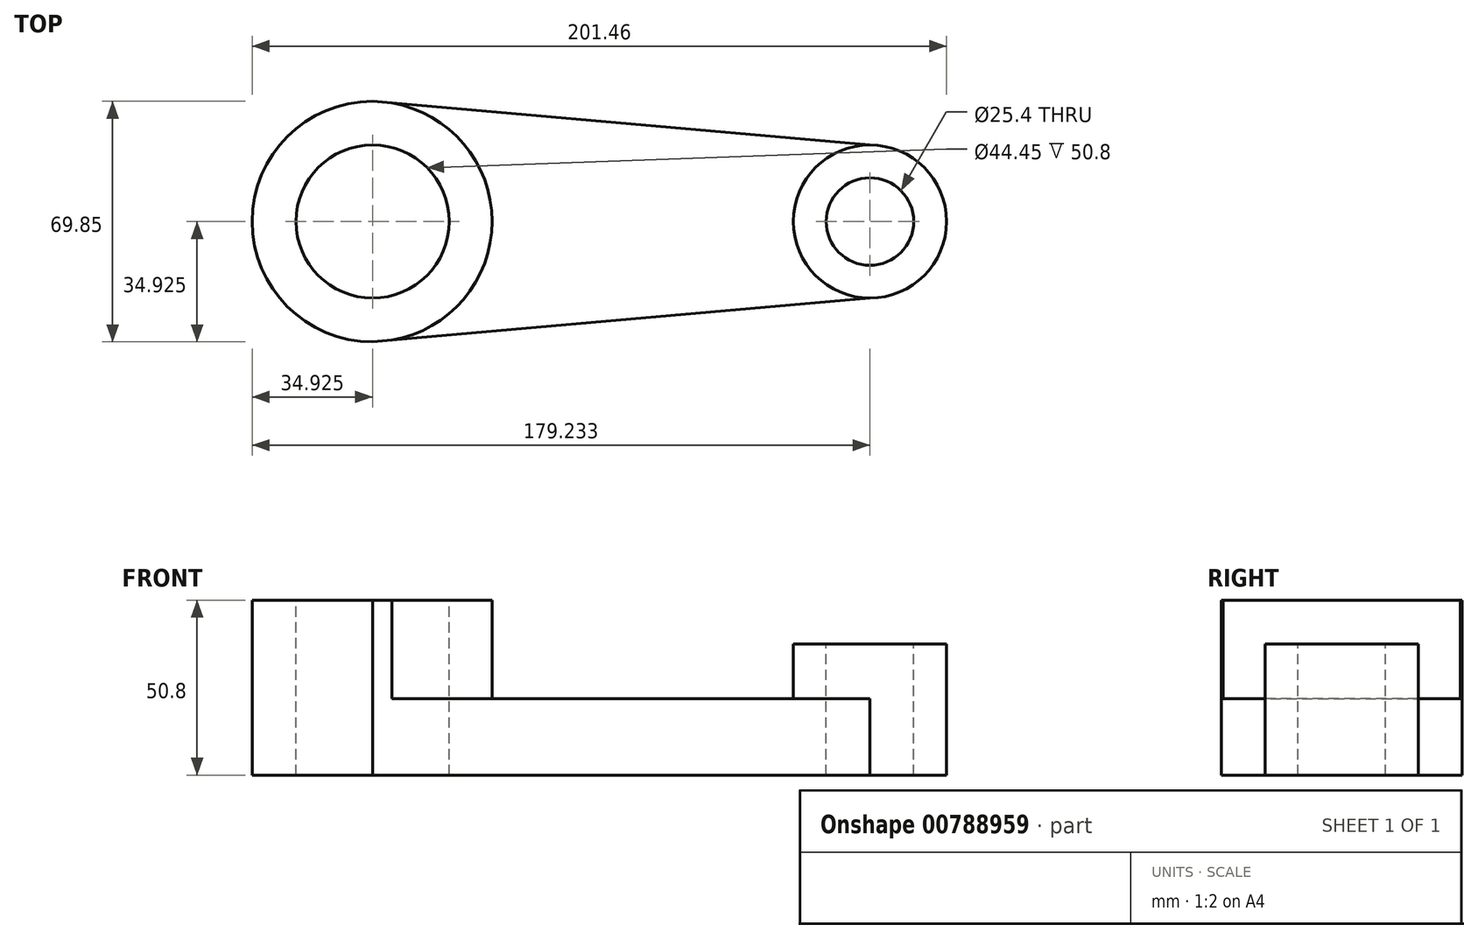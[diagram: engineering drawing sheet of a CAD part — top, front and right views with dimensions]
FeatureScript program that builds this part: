
annotation { "Feature Type Name" : "Feature", "Feature Type Description" : "" }
export const myFeature = defineFeature(function(context is Context, id is Id, definition is map)
    precondition{}
    {
        {
            var Q0;
            Q0=qCreatedBy(makeId("Front.planeOp"),FACE);
            var sketch = newSketch(context, id + "F0", { "sketchPlane" : qUnion([Q0])});
            skLineSegment(sketch, "E0", {"start": v(0, 0) * mm, "end": v(177.8, 0) * mm});
            skLineSegment(sketch, "E1", {"start": v(177.8, 0) * mm, "end": v(177.8, 50.8) * mm});
            skLineSegment(sketch, "E2", {"start": v(177.8, 50.8) * mm, "end": v(0, 50.8) * mm});
            skLineSegment(sketch, "E3", {"start": v(0, 50.8) * mm, "end": v(0, 0) * mm});
            skSolve(sketch);
        }
        {
            var Q0;
            Q0=makeQuery(id+"F0.imprint","IMPRINT",FACE,{"disambiguationData":[TD([[makeQuery(id+"F0.imprint","IMPRINT",EDGE,{"derivedFrom":sQuery(id+"F0.wireOp",EDGE,"E0")}),1.0]])]});
            extrude(context, id + "F1", {"entities" : qUnion([Q0]), "depth" : 69.85 * mm, "offsetDistance" : 25.4 * mm});
        }
        {
            var Q0;
            Q0=makeQuery(id+"F1.opExtrude","SWEPT_FACE",FACE,{"disambiguationData":[OSD([sQuery(id+"F0.wireOp",EDGE,"E2")])]});
            var sketch = newSketch(context, id + "F2", { "sketchPlane" : qUnion([Q0])});
            skLineSegment(sketch, "E4", {"start": v(0, -34.93) * mm, "end": v(34.93, -34.93) * mm, "construction": true});
            skCircle(sketch, "E5", {"center": v(34.93, -34.93) * mm, "radius": 34.93 * mm});
            skCircle(sketch, "E6", {"center": v(34.93, -34.93) * mm, "radius": 22.23 * mm});
            skSolve(sketch);
        }
        {
            var Q0;
            {var subQ0=sQuery(id+"F2.wireOp",EDGE,"E5");var subQ1=sQuery(id+"F0.wireOp",EDGE,"E2");var subQ4=makeQuery(id+"F1.opExtrude","CAP_EDGE",EDGE,{"disambiguationData":[OSD([subQ1])],"isStart":false});var subQ5=makeQuery(id+"F2.imprint","INTERSECT",VERTEX,{"derivedFrom":[subQ4,subQ0]});Q0=makeQuery(id+"F2.imprint","IMPRINT",FACE,{"disambiguationData":[TD([[makeQuery(id+"F2.imprint","IMPRINT",EDGE,{"disambiguationData":[TD([[subQ5,1.0]])],"derivedFrom":subQ0}),-1.0]])]});}
            var Q1;
            {var subQ0=sQuery(id+"F2.wireOp",EDGE,"E5");var subQ1=sQuery(id+"F0.wireOp",EDGE,"E2");var subQ4=makeQuery(id+"F1.opExtrude","CAP_EDGE",EDGE,{"disambiguationData":[OSD([subQ1])],"isStart":true});var subQ5=makeQuery(id+"F2.imprint","INTERSECT",VERTEX,{"derivedFrom":[subQ4,subQ0]});Q1=makeQuery(id+"F2.imprint","IMPRINT",FACE,{"disambiguationData":[TD([[makeQuery(id+"F2.imprint","IMPRINT",EDGE,{"disambiguationData":[TD([[subQ5,-1.0]])],"derivedFrom":subQ0}),-1.0]])]});}
            extrude(context, id + "F3", {"entities" : qUnion([Q0, Q1]), "operationType" : NewBodyOperationType.REMOVE, "endBound" : BoundingType.UP_TO_NEXT, "oppositeDirection" : true, "depth" : 50.8 * mm, "offsetDistance" : 25.4 * mm});
        }
        {
            var Q0;
            Q0=makeQuery(id+"F2.imprint","IMPRINT",FACE,{"disambiguationData":[TD([[makeQuery(id+"F2.imprint","IMPRINT",EDGE,{"derivedFrom":sQuery(id+"F2.wireOp",EDGE,"E6")}),1.0]])]});
            extrude(context, id + "F4", {"entities" : qUnion([Q0]), "operationType" : NewBodyOperationType.REMOVE, "endBound" : BoundingType.UP_TO_NEXT, "oppositeDirection" : true, "depth" : 25.4 * mm, "offsetDistance" : 25.4 * mm});
        }
        {
            var Q0;
            Q0=makeQuery(id+"F1.opExtrude","SWEPT_FACE",FACE,{"disambiguationData":[OSD([sQuery(id+"F0.wireOp",EDGE,"E1")])]});
            extrude(context, id + "F5", {"entities" : qUnion([Q0]), "operationType" : NewBodyOperationType.ADD, "depth" : 50.8 * mm, "offsetDistance" : 25.4 * mm});
        }
        {
            var Q0;
            {var subQ0=sQuery(id+"F0.wireOp",EDGE,"E2");Q0=makeQuery(id+"F5.boolean.opBoolean","MERGE",FACE,{"derivedFrom":[makeQuery(id+"F1.opExtrude","SWEPT_FACE",FACE,{"disambiguationData":[OSD([subQ0])]}),makeQuery(id+"F5.opExtrude","SWEPT_FACE",FACE,{"disambiguationData":[OSD([sQuery(id+"F0.wireOp",EDGE,"E1"),subQ0])]})]});}
            var sketch = newSketch(context, id + "F6", { "sketchPlane" : qUnion([Q0])});
            skLineSegment(sketch, "E7", {"start": v(34.92, 0) * mm, "end": v(180.98, -10.35) * mm});
            skLineSegment(sketch, "E8", {"start": v(34.92, -69.85) * mm, "end": v(180.98, -59.5) * mm});
            skArc(sketch, "E9", {"start": v(180.98, -59.5) * mm, "mid": v(203.87, -34.92) * mm, "end": v(180.98, -10.35) * mm});
            skCircle(sketch, "E10", {"center": v(179.23, -34.92) * mm, "radius": 12.7 * mm});
            skSolve(sketch);
        }
        {
            var Q0;
            {var subQ0=sQuery(id+"F6.wireOp",EDGE,"E9");Q0=makeQuery(id+"F6.imprint","IMPRINT",FACE,{"disambiguationData":[TD([[makeQuery(id+"F6.imprint","IMPRINT",EDGE,{"derivedFrom":subQ0}),-1.0]])]});}
            extrude(context, id + "F7", {"entities" : qUnion([Q0]), "operationType" : NewBodyOperationType.REMOVE, "endBound" : BoundingType.UP_TO_NEXT, "oppositeDirection" : true, "depth" : 50.8 * mm, "offsetDistance" : 25.4 * mm});
        }
        {
            var Q0;
            Q0 = qSketchRegion(id + "F6", true);
            extrude(context, id + "F8", {"entities" : qUnion([Q0]), "operationType" : NewBodyOperationType.REMOVE, "endBound" : BoundingType.UP_TO_NEXT, "oppositeDirection" : true, "depth" : 25.4 * mm, "offsetDistance" : 25.4 * mm});
        }
        {
            var Q0;
            {var subQ0=sQuery(id+"F0.wireOp",EDGE,"E2");Q0=makeQuery(id+"F5.boolean.opBoolean","MERGE",FACE,{"derivedFrom":[makeQuery(id+"F1.opExtrude","SWEPT_FACE",FACE,{"disambiguationData":[OSD([subQ0])]}),makeQuery(id+"F5.opExtrude","SWEPT_FACE",FACE,{"disambiguationData":[OSD([sQuery(id+"F0.wireOp",EDGE,"E1"),subQ0])]})]});}
            var sketch = newSketch(context, id + "F9", { "sketchPlane" : qUnion([Q0])});
            skCircle(sketch, "E11", {"center": v(179.23, -34.92) * mm, "radius": 22.23 * mm});
            skLineSegment(sketch, "E12", {"start": v(34.93, 0) * mm, "end": v(179.23, -12.7) * mm});
            skLineSegment(sketch, "E13", {"start": v(34.93, -69.85) * mm, "end": v(179.23, -57.15) * mm});
            skSolve(sketch);
        }
        {
            var Q0;
            {var subQ1=sQuery(id+"F9.wireOp",EDGE,"E12");Q0=makeQuery(id+"F9.imprint","IMPRINT",FACE,{"disambiguationData":[TD([[makeQuery(id+"F9.imprint","IMPRINT",EDGE,{"derivedFrom":subQ1}),1.0]])]});}
            extrude(context, id + "F10", {"entities" : qUnion([Q0]), "operationType" : NewBodyOperationType.REMOVE, "endBound" : BoundingType.UP_TO_NEXT, "oppositeDirection" : true, "depth" : 25.4 * mm, "offsetDistance" : 25.4 * mm});
        }
        {
            var Q0;
            {var subQ0=sQuery(id+"F0.wireOp",EDGE,"E2");Q0=makeQuery(id+"F5.boolean.opBoolean","MERGE",FACE,{"derivedFrom":[makeQuery(id+"F1.opExtrude","SWEPT_FACE",FACE,{"disambiguationData":[OSD([subQ0])]}),makeQuery(id+"F5.opExtrude","SWEPT_FACE",FACE,{"disambiguationData":[OSD([sQuery(id+"F0.wireOp",EDGE,"E1"),subQ0])]})]});}
            var sketch = newSketch(context, id + "F11", { "sketchPlane" : qUnion([Q0])});
            skArc(sketch, "E14", {"start": v(34.93, -69.85) * mm, "mid": v(69.58, -34.93) * mm, "end": v(34.93, 0) * mm});
            skCircle(sketch, "E15", {"center": v(179.23, -34.92) * mm, "radius": 22.23 * mm});
            skSolve(sketch);
        }
        {
            var Q0;
            {var subQ0=sQuery(id+"F11.wireOp",EDGE,"E14");var subQ1=makeQuery(id+"F10.boolean.opBoolean","COPY",EDGE,{"derivedFrom":makeQuery(id+"F10.opExtrude","CAP_EDGE",EDGE,{"disambiguationData":[OSD([sQuery(id+"F9.wireOp",EDGE,"E13")])],"isStart":true})});var subQ2=makeQuery(id+"F11.imprint","INTERSECT",VERTEX,{"derivedFrom":[subQ1,subQ0]});Q0=makeQuery(id+"F11.imprint","IMPRINT",FACE,{"disambiguationData":[TD([[makeQuery(id+"F11.imprint","IMPRINT",EDGE,{"disambiguationData":[TD([[subQ2,-1.0]])],"derivedFrom":subQ0}),-1.0]])]});}
            extrude(context, id + "F12", {"entities" : qUnion([Q0]), "operationType" : NewBodyOperationType.REMOVE, "oppositeDirection" : true, "depth" : 28.57 * mm, "offsetDistance" : 25.4 * mm});
        }
        {
            var Q0;
            {var subQ0=sQuery(id+"F0.wireOp",EDGE,"E2");Q0=makeQuery(id+"F12.boolean.opBoolean","SPLIT",FACE,{"disambiguationData":[TD([makeQuery(id+"F8.boolean.opBoolean","COPY",FACE,{"derivedFrom":makeQuery(id+"F8.opExtrude","SWEPT_FACE",FACE,{"disambiguationData":[OSD([sQuery(id+"F6.wireOp",EDGE,"E10")])]})})])],"derivedFrom":makeQuery(id+"F5.boolean.opBoolean","MERGE",FACE,{"derivedFrom":[makeQuery(id+"F1.opExtrude","SWEPT_FACE",FACE,{"disambiguationData":[OSD([subQ0])]}),makeQuery(id+"F5.opExtrude","SWEPT_FACE",FACE,{"disambiguationData":[OSD([sQuery(id+"F0.wireOp",EDGE,"E1"),subQ0])]})]})});}
            var sketch = newSketch(context, id + "F13", { "sketchPlane" : qUnion([Q0])});
            skCircle(sketch, "E16", {"center": v(179.23, -34.92) * mm, "radius": 22.23 * mm});
            skSolve(sketch);
        }
        {
            var Q0;
            Q0 = qSketchRegion(id + "F13", true);
            extrude(context, id + "F14", {"entities" : qUnion([Q0]), "operationType" : NewBodyOperationType.REMOVE, "oppositeDirection" : true, "depth" : 12.7 * mm, "offsetDistance" : 25.4 * mm});
        }
    });
